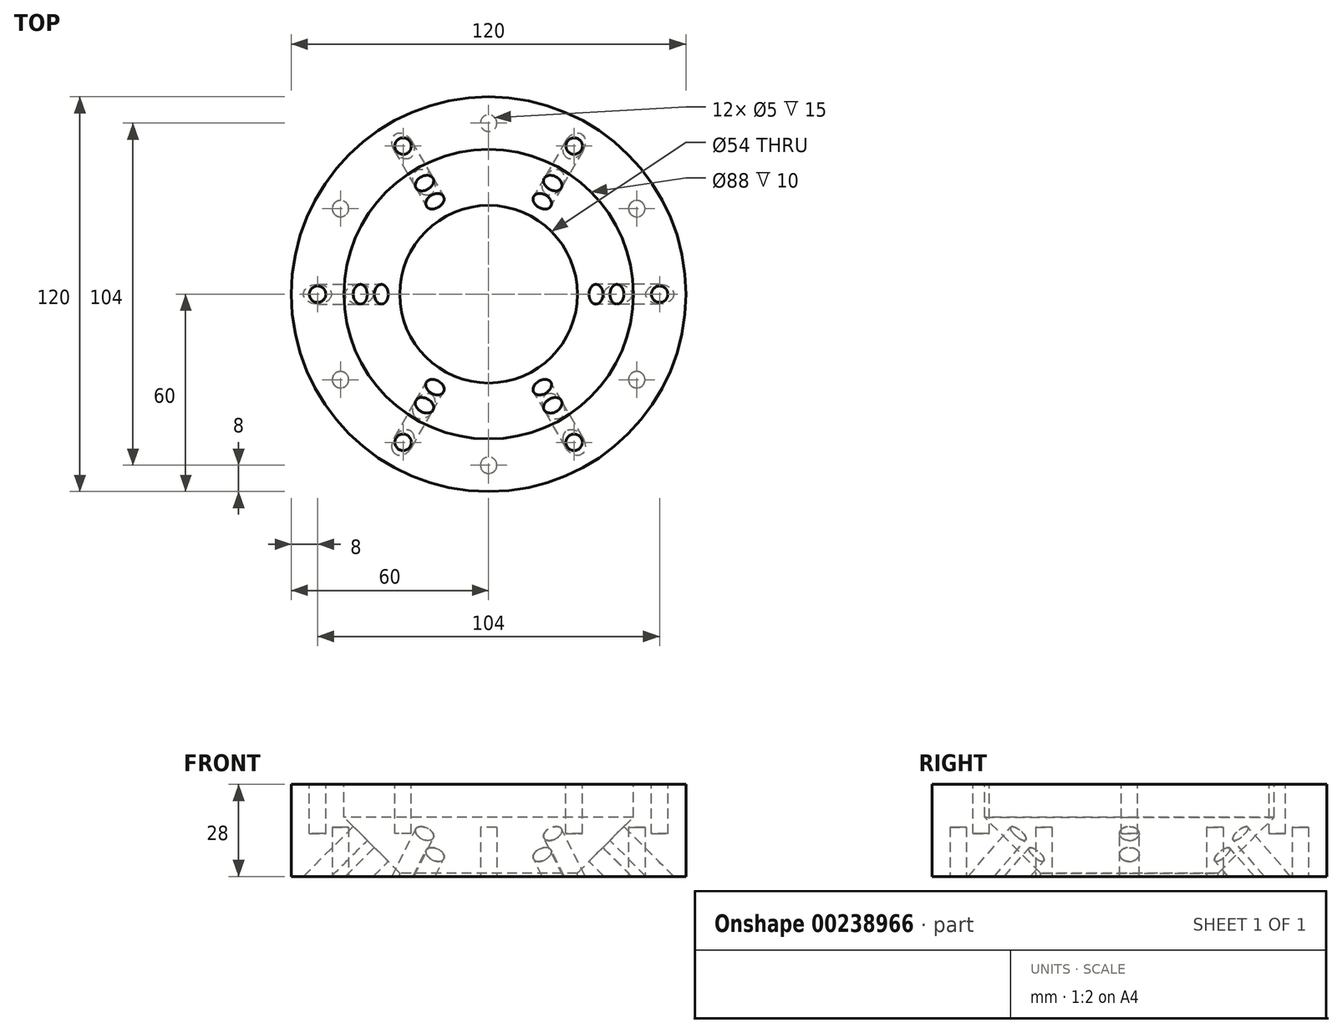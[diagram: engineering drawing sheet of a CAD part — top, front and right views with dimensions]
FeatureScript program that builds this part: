
annotation { "Feature Type Name" : "Feature", "Feature Type Description" : "" }
export const myFeature = defineFeature(function(context is Context, id is Id, definition is map)
    precondition{}
    {
        {
            var Q0;
            Q0=qCreatedBy(makeId("Front.planeOp"),FACE);
            var sketch = newSketch(context, id + "F0", { "sketchPlane" : qUnion([Q0])});
            skLineSegment(sketch, "E0", {"start": v(0, 70.12) * mm, "end": v(0, -51.14) * mm, "construction": true});
            skLineSegment(sketch, "E1", {"start": v(-40, -25.13) * mm, "end": v(-40, -82.12) * mm, "construction": true});
            skLineSegment(sketch, "E2", {"start": v(-33.5, -13) * mm, "end": v(-33.5, -83.09) * mm, "construction": true});
            skLineSegment(sketch, "E3", {"start": v(-55, -23.79) * mm, "end": v(-55, -71.7) * mm, "construction": true});
            skPoint(sketch, "E4", {"position": v(-45, -20) * mm});
            skLineSegment(sketch, "E5", {"start": v(-27, -2) * mm, "end": v(-44, 15) * mm});
            skLineSegment(sketch, "E6", {"start": v(-44, 20) * mm, "end": v(0, 20) * mm, "construction": true});
            skLineSegment(sketch, "E7.trimOffspring", {"start": v(-44, 15) * mm, "end": v(-44, 25) * mm});
            skLineSegment(sketch, "E8", {"start": v(0, 20) * mm, "end": v(0, -2) * mm});
            skLineSegment(sketch, "E9", {"start": v(-15, -3) * mm, "end": v(-15, -14) * mm});
            skLineSegment(sketch, "E10.trimOffspring", {"start": v(-44, 25) * mm, "end": v(-60, 25) * mm});
            skLineSegment(sketch, "E11", {"start": v(-27, -14) * mm, "end": v(-60, -14) * mm, "construction": true});
            skLineSegment(sketch, "E12", {"start": v(-44, -3) * mm, "end": v(-26, -3) * mm});
            skLineSegment(sketch, "E13", {"start": v(-60.56, -2) * mm, "end": v(-7.47, -2) * mm, "construction": true});
            skLineSegment(sketch, "E14", {"start": v(-32.2, -0.13) * mm, "end": v(-20.33, 11.74) * mm, "construction": true});
            skLineSegment(sketch, "E15", {"start": v(-37.48, 3.07) * mm, "end": v(-25.45, 15.1) * mm, "construction": true});
            skLineSegment(sketch, "E16", {"start": v(-39.45, 6.77) * mm, "end": v(-29.58, 16.63) * mm, "construction": true});
            skLineSegment(sketch, "E17", {"start": v(-44.65, 10.05) * mm, "end": v(-35.06, 19.64) * mm, "construction": true});
            skPoint(sketch, "E18", {"position": v(-27, -2) * mm});
            skLineSegment(sketch, "E19", {"start": v(-27, -2) * mm, "end": v(-16.61, 8.39) * mm, "construction": true});
            skLineSegment(sketch, "E20", {"start": v(-60, 25) * mm, "end": v(-60, -3) * mm});
            skLineSegment(sketch, "E21", {"start": v(-27, -2) * mm, "end": v(-27, -3) * mm});
            skLineSegment(sketch, "E22", {"start": v(-44, -3) * mm, "end": v(-44, -3) * mm});
            skLineSegment(sketch, "E23", {"start": v(-67.6, -3) * mm, "end": v(-41.15, -3) * mm});
            skSolve(sketch);
        }
        {
            var Q0;
            Q0=makeQuery(id+"F0.imprint","IMPRINT",FACE,{"disambiguationData":[TD([[makeQuery(id+"F0.imprint","IMPRINT",EDGE,{"derivedFrom":sQuery(id+"F0.wireOp",EDGE,"E5")}),1.0]])]});
            var Q1;
            Q1=sQuery(id+"F0.wireOp",EDGE,"E8");
            revolve(context, id + "F1", {"entities" : qUnion([Q0]), "axis" : qUnion([Q1]), "revolveType" : RevolveType.FULL});
        }
        {
            var Q0;
            Q0=makeQuery(id+"F1.opRevolve","SWEPT_FACE",FACE,{"disambiguationData":[OSD([sQuery(id+"F0.wireOp",EDGE,"E12"),sQuery(id+"F0.wireOp",EDGE,"E23")])]});
            cPlane(context, id + "F2", {"entities" : qUnion([Q0]), "cplaneType" : CPlaneType.OFFSET, "offset" : 0 * mm, "width" : 150 * mm, "height" : 150 * mm});
        }
        {
            var Q0;
            Q0=qCreatedBy(id+"F2.planeOp",FACE);
            var sketch = newSketch(context, id + "F3", { "sketchPlane" : qUnion([Q0])});
            skCircle(sketch, "E24", {"center": v(0, 0) * mm, "radius": 52 * mm, "construction": true});
            skCircle(sketch, "E25", {"center": v(0, -52) * mm, "radius": 2.5 * mm});
            skSolve(sketch);
        }
        {
            var Q0;
            Q0 = qSketchRegion(id + "F3", true);
            extrude(context, id + "F4", {"entities" : qUnion([Q0]), "oppositeDirection" : true, "depth" : 15 * mm, "hasSecondDirection" : true, "secondDirectionOppositeDirection" : false, "secondDirectionDepth" : 20 * mm});
        }
        {
            var Q0;
            Q0=makeQuery(id+"F4.opExtrude","SWEPT_BODY",BODY,{"disambiguationData":[OSD([sQuery(id+"F3.wireOp",EDGE,"E25")])]});
            var Q1;
            Q1=sQuery(id+"F0.wireOp",EDGE,"E8");
            circularPattern(context, id + "F5", {"operationType" : NewBodyOperationType.REMOVE, "entities" : qUnion([Q0]), "axis" : qUnion([Q1]), "angle" : 360 * degree, "instanceCount" : 6, "oppositeDirection" : true, "equalSpace" : true});
        }
        {
            var Q0;
            Q0=makeQuery(id+"F1.opRevolve","SWEPT_FACE",FACE,{"disambiguationData":[OSD([sQuery(id+"F0.wireOp",EDGE,"E10.trimOffspring")])]});
            cPlane(context, id + "F6", {"entities" : qUnion([Q0]), "cplaneType" : CPlaneType.OFFSET, "offset" : 0 * mm, "width" : 150 * mm, "height" : 150 * mm});
        }
        {
            var Q0;
            Q0=qCreatedBy(id+"F6.planeOp",FACE);
            var sketch = newSketch(context, id + "F7", { "sketchPlane" : qUnion([Q0])});
            skLineSegment(sketch, "E26", {"start": v(0, 0) * mm, "end": v(-39.92, 69.14) * mm, "construction": true});
            skCircle(sketch, "E27", {"center": v(0, 0) * mm, "radius": 52 * mm, "construction": true});
            skCircle(sketch, "E28", {"center": v(-26, 45.03) * mm, "radius": 2.5 * mm});
            skSolve(sketch);
        }
        {
            var Q0;
            Q0 = qSketchRegion(id + "F7", true);
            extrude(context, id + "F8", {"entities" : qUnion([Q0]), "oppositeDirection" : true, "depth" : 15 * mm, "hasSecondDirection" : true, "secondDirectionOppositeDirection" : false, "secondDirectionDepth" : 20 * mm});
        }
        {
            var Q0;
            Q0=makeQuery(id+"F8.opExtrude","SWEPT_BODY",BODY,{"disambiguationData":[OSD([sQuery(id+"F7.wireOp",EDGE,"E28")])]});
            var Q1;
            Q1=sQuery(id+"F0.wireOp",EDGE,"E0");
            circularPattern(context, id + "F9", {"operationType" : NewBodyOperationType.REMOVE, "entities" : qUnion([Q0]), "axis" : qUnion([Q1]), "angle" : 360 * degree, "instanceCount" : 6, "equalSpace" : true});
        }
        {
            var Q0;
            Q0=qCreatedBy(id+"F6.planeOp",FACE);
            var sketch = newSketch(context, id + "F10", { "sketchPlane" : qUnion([Q0])});
            skLineSegment(sketch, "E29", {"start": v(0, 0) * mm, "end": v(-39.56, 68.51) * mm, "construction": true});
            skPoint(sketch, "E30", {"position": v(-39.56, 68.51) * mm});
            skPoint(sketch, "E31", {"position": v(0, 0) * mm});
            skSolve(sketch);
        }
        {
            var Q0;
            Q0=sQuery(id+"F10.wireOp",VERTEX,"E30");
            var Q1;
            Q1=sQuery(id+"F0.wireOp",EDGE,"E0");
            cPlane(context, id + "F11", {"entities" : qUnion([Q0, Q1]), "cplaneType" : CPlaneType.LINE_ANGLE, "offset" : 25 * mm, "angle" : 0 * degree, "width" : 150 * mm, "height" : 150 * mm});
        }
        {
            var Q0;
            Q0=qCreatedBy(id+"F11.planeOp",FACE);
            var sketch = newSketch(context, id + "F12", { "sketchPlane" : qUnion([Q0])});
            skLineSegment(sketch, "E32.0", {"start": v(-55, 5.81) * mm, "end": v(-55, -71.7) * mm, "construction": true});
            skLineSegment(sketch, "E33.0", {"start": v(-33.5, 8.98) * mm, "end": v(-33.5, -83.09) * mm, "construction": true});
            skLineSegment(sketch, "E34", {"start": v(-30.26, 18.78) * mm, "end": v(-67.4, -18.36) * mm});
            skLineSegment(sketch, "E35", {"start": v(-32.38, 20.9) * mm, "end": v(-30.26, 18.78) * mm});
            skLineSegment(sketch, "E36", {"start": v(-69.53, -16.24) * mm, "end": v(-67.4, -18.36) * mm});
            skLineSegment(sketch, "E37.0", {"start": v(-27, -2) * mm, "end": v(-16.61, 8.39) * mm, "construction": true});
            skLineSegment(sketch, "E38.0", {"start": v(-27, -2) * mm, "end": v(-44, 15) * mm, "construction": true});
            skLineSegment(sketch, "E39", {"start": v(-32.38, 20.9) * mm, "end": v(-69.53, -16.24) * mm});
            skPoint(sketch, "E40", {"position": v(0, 0) * mm});
            skSolve(sketch);
        }
        {
            var Q0;
            Q0 = qSketchRegion(id + "F12", true);
            var Q1;
            Q1=sQuery(id+"F12.wireOp",EDGE,"E34");
            revolve(context, id + "F13", {"entities" : qUnion([Q0]), "axis" : qUnion([Q1]), "revolveType" : RevolveType.FULL});
        }
        {
            var Q0;
            Q0=qCreatedBy(id+"F11.planeOp",FACE);
            var sketch = newSketch(context, id + "F14", { "sketchPlane" : qUnion([Q0])});
            skLineSegment(sketch, "E41.0", {"start": v(-27, -2) * mm, "end": v(-44, 15) * mm, "construction": true});
            skLineSegment(sketch, "E42", {"start": v(-17.75, 18.57) * mm, "end": v(-54.69, -18.37) * mm});
            skLineSegment(sketch, "E43", {"start": v(-19.87, 20.69) * mm, "end": v(-17.75, 18.57) * mm});
            skLineSegment(sketch, "E44", {"start": v(-56.75, -16.2) * mm, "end": v(-54.63, -18.31) * mm});
            skLineSegment(sketch, "E45", {"start": v(-19.87, 20.69) * mm, "end": v(-56.75, -16.2) * mm});
            skPoint(sketch, "E46", {"position": v(0, 0) * mm});
            skSolve(sketch);
        }
        {
            var Q0;
            Q0 = qSketchRegion(id + "F14", true);
            var Q1;
            Q1=sQuery(id+"F14.wireOp",EDGE,"E42");
            revolve(context, id + "F15", {"entities" : qUnion([Q0]), "axis" : qUnion([Q1]), "revolveType" : RevolveType.FULL});
        }
        {
            var Q0;
            Q0=makeQuery(id+"F13.opRevolve","SWEPT_BODY",BODY,{"disambiguationData":[OSD([sQuery(id+"F12.wireOp",EDGE,"E34"),sQuery(id+"F12.wireOp",EDGE,"E35"),sQuery(id+"F12.wireOp",EDGE,"E36"),sQuery(id+"F12.wireOp",EDGE,"E39")])]});
            var Q1;
            Q1=makeQuery(id+"F15.opRevolve","SWEPT_BODY",BODY,{"disambiguationData":[OSD([sQuery(id+"F14.wireOp",EDGE,"E42"),sQuery(id+"F14.wireOp",EDGE,"E43"),sQuery(id+"F14.wireOp",EDGE,"E44"),sQuery(id+"F14.wireOp",EDGE,"E45")])]});
            var Q2;
            Q2=sQuery(id+"F0.wireOp",EDGE,"E0");
            circularPattern(context, id + "F16", {"operationType" : NewBodyOperationType.REMOVE, "entities" : qUnion([Q0, Q1]), "axis" : qUnion([Q2]), "angle" : 360 * degree, "instanceCount" : 6, "equalSpace" : true});
        }
    });
